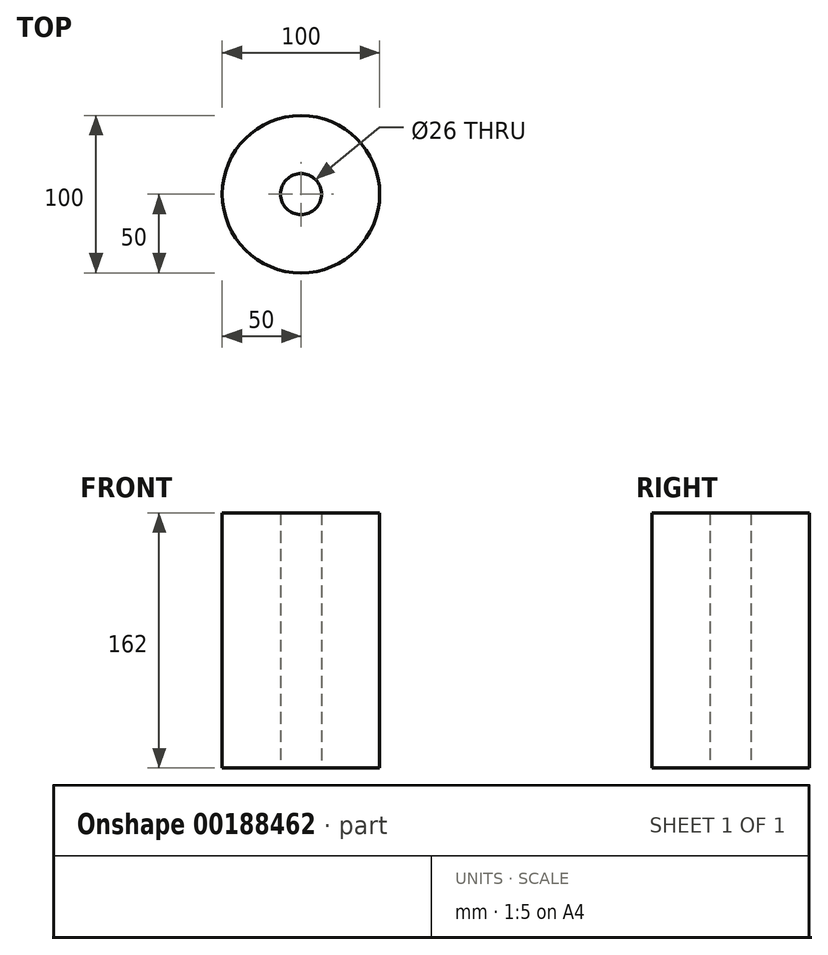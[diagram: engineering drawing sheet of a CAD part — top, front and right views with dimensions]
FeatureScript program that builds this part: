
annotation { "Feature Type Name" : "Feature", "Feature Type Description" : "" }
export const myFeature = defineFeature(function(context is Context, id is Id, definition is map)
    precondition{}
    {
        {
            var Q0;
            Q0=qCreatedBy(makeId("Top.planeOp"),FACE);
            var sketch = newSketch(context, id + "F0", { "sketchPlane" : qUnion([Q0])});
            skCircle(sketch, "E0", {"center": v(0, 0) * mm, "radius": 50 * mm});
            skCircle(sketch, "E1", {"center": v(0, 0) * mm, "radius": 13 * mm});
            skSolve(sketch);
        }
        {
            var Q0;
            Q0 = qSketchRegion(id + "F0", true);
            extrude(context, id + "F1", {"entities" : qUnion([Q0]), "depth" : 162 * mm});
        }
    });
